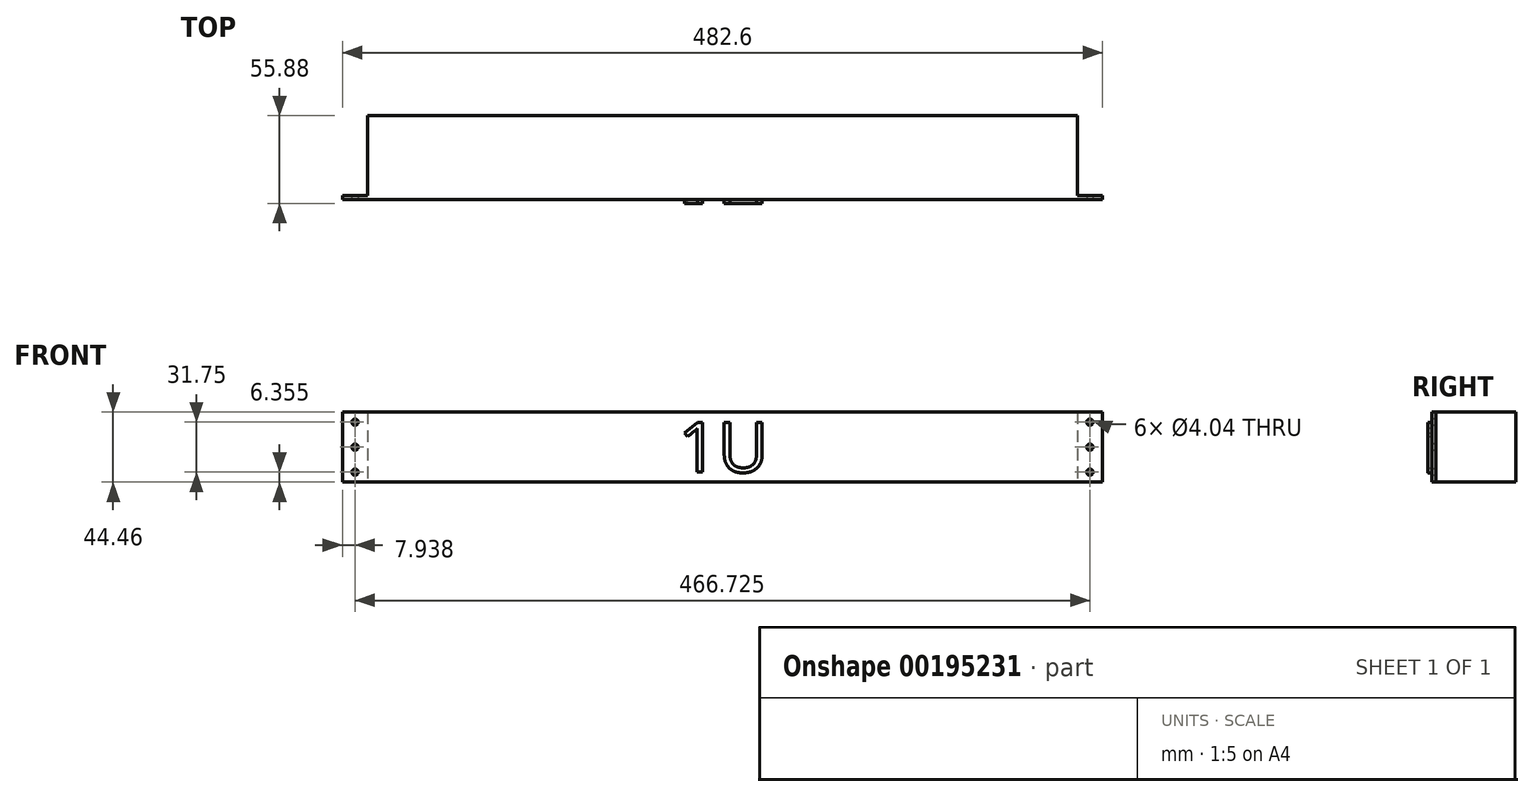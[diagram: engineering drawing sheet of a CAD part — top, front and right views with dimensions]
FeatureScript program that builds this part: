
annotation { "Feature Type Name" : "Feature", "Feature Type Description" : "" }
export const myFeature = defineFeature(function(context is Context, id is Id, definition is map)
    precondition{}
    {
        {
            var Q0;
            Q0=qCreatedBy(makeId("Front.planeOp"),FACE);
            var sketch = newSketch(context, id + "F0", { "sketchPlane" : qUnion([Q0])});
            skLineSegment(sketch, "E0.bottom", {"start": v(-241.3, 22.22) * mm, "end": v(241.3, 22.22) * mm});
            skLineSegment(sketch, "E0.top", {"start": v(-241.3, -22.22) * mm, "end": v(241.3, -22.22) * mm});
            skLineSegment(sketch, "E0.left", {"start": v(-241.3, 22.22) * mm, "end": v(-241.3, -22.22) * mm});
            skLineSegment(sketch, "E0.right", {"start": v(241.3, 22.22) * mm, "end": v(241.3, -22.22) * mm});
            skPoint(sketch, "E0.middle", {"position": v(0, 0) * mm});
            skSolve(sketch);
        }
        {
            var Q0;
            Q0 = qSketchRegion(id + "F0", true);
            extrude(context, id + "F1", {"entities" : qUnion([Q0]), "depth" : 2.54 * mm});
        }
        {
            var Q0;
            Q0=makeQuery(id+"F1.opExtrude","CAP_FACE",FACE,{"disambiguationData":[OSD([sQuery(id+"F0.wireOp",EDGE,"E0.bottom"),sQuery(id+"F0.wireOp",EDGE,"E0.top"),sQuery(id+"F0.wireOp",EDGE,"E0.left"),sQuery(id+"F0.wireOp",EDGE,"E0.right")])],"isStart":true});
            var sketch = newSketch(context, id + "F2", { "sketchPlane" : qUnion([Q0])});
            skLineSegment(sketch, "E1.bottom", {"start": v(-225.43, 22.22) * mm, "end": v(225.42, 22.23) * mm});
            skLineSegment(sketch, "E1.top", {"start": v(-225.43, -22.23) * mm, "end": v(225.42, -22.23) * mm});
            skLineSegment(sketch, "E1.left", {"start": v(-225.43, 22.22) * mm, "end": v(-225.43, -22.23) * mm});
            skLineSegment(sketch, "E1.right", {"start": v(225.43, 22.23) * mm, "end": v(225.43, -22.23) * mm});
            skPoint(sketch, "E1.middle", {"position": v(0, 0) * mm});
            skSolve(sketch);
        }
        {
            var Q0;
            Q0 = qSketchRegion(id + "F2", true);
            extrude(context, id + "F3", {"entities" : qUnion([Q0]), "operationType" : NewBodyOperationType.ADD, "depth" : 50.8 * mm});
        }
        {
            var Q0;
            Q0=makeQuery(id+"F1.opExtrude","CAP_FACE",FACE,{"disambiguationData":[OSD([sQuery(id+"F0.wireOp",EDGE,"E0.bottom"),sQuery(id+"F0.wireOp",EDGE,"E0.top"),sQuery(id+"F0.wireOp",EDGE,"E0.left"),sQuery(id+"F0.wireOp",EDGE,"E0.right")])],"isStart":false});
            var sketch = newSketch(context, id + "F4", { "sketchPlane" : qUnion([Q0])});
            skPoint(sketch, "E2", {"position": v(-233.36, 15.87) * mm});
            skPoint(sketch, "E3", {"position": v(-233.36, 0) * mm});
            skPoint(sketch, "E4", {"position": v(-233.36, -15.88) * mm});
            skPoint(sketch, "E5.0.1.0", {"position": v(-233.36, -28.58) * mm});
            skPoint(sketch, "E5.0.1.1", {"position": v(-233.36, -44.45) * mm});
            skPoint(sketch, "E5.0.1.2", {"position": v(-233.36, -60.33) * mm});
            skPoint(sketch, "E5.1.0.0", {"position": v(233.36, 15.87) * mm});
            skPoint(sketch, "E5.1.0.1", {"position": v(233.36, 0) * mm});
            skPoint(sketch, "E5.1.0.2", {"position": v(233.36, -15.88) * mm});
            skPoint(sketch, "E5.1.1.0", {"position": v(233.36, -28.58) * mm});
            skPoint(sketch, "E5.1.1.1", {"position": v(233.36, -44.45) * mm});
            skPoint(sketch, "E5.1.1.2", {"position": v(233.36, -60.33) * mm});
            skLineSegment(sketch, "E5.direction1", {"start": v(-233.36, 15.87) * mm, "end": v(233.36, 15.87) * mm, "construction": true});
            skLineSegment(sketch, "E5.direction2", {"start": v(-233.36, 15.87) * mm, "end": v(-233.36, -28.58) * mm, "construction": true});
            skSolve(sketch);
        }
        {
            var Q0;
            Q0=sQuery(id+"F4.wireOp",VERTEX,"E5.0.1.1");
            var Q1;
            Q1=sQuery(id+"F4.wireOp",VERTEX,"E5.0.1.2");
            var Q2;
            Q2=sQuery(id+"F4.wireOp",VERTEX,"E5.1.0.0");
            var Q3;
            Q3=sQuery(id+"F4.wireOp",VERTEX,"E5.1.1.0");
            var Q4;
            Q4=sQuery(id+"F4.wireOp",VERTEX,"E5.1.1.1");
            var Q5;
            Q5=sQuery(id+"F4.wireOp",VERTEX,"E5.1.0.1");
            var Q6;
            Q6=sQuery(id+"F4.wireOp",VERTEX,"E5.1.1.2");
            var Q7;
            Q7=sQuery(id+"F4.wireOp",VERTEX,"E5.1.0.2");
            var Q8;
            Q8=sQuery(id+"F4.wireOp",VERTEX,"E2");
            var Q9;
            Q9=sQuery(id+"F4.wireOp",VERTEX,"E3");
            var Q10;
            Q10=sQuery(id+"F4.wireOp",VERTEX,"E4");
            var Q11;
            Q11=sQuery(id+"F4.wireOp",VERTEX,"E5.0.1.0");
            var Q12;
            Q12=makeQuery(id+"F1.opExtrude","SWEPT_BODY",BODY,{"disambiguationData":[OSD([sQuery(id+"F0.wireOp",EDGE,"E0.bottom"),sQuery(id+"F0.wireOp",EDGE,"E0.top"),sQuery(id+"F0.wireOp",EDGE,"E0.left"),sQuery(id+"F0.wireOp",EDGE,"E0.right")])]});
            hole(context, id + "F5", {"style" : HoleStyle.SIMPLE, "endStyle" : HoleEndStyle.THROUGH, "standardTappedOrClearance" : lookupTablePath({ "standard" : "ANSI", "engagement" : "75%", "pitch" : "32 tpi", "size" : "#10", "type" : "Tapped" }), "standardBlindInLast" : lookupTablePath({ "standard" : "ANSI", "engagement" : "75%", "pitch" : "32 tpi", "size" : "#10", "type" : "Tapped" }), "holeDiameter" : 4.04 * mm, "locations" : qUnion([Q0, Q1, Q2, Q3, Q4, Q5, Q6, Q7, Q8, Q9, Q10, Q11]), "scope" : qUnion([Q12]), "isTappedThrough" : true, "majorDiameter" : 4.83 * mm, "showTappedDepth" : true});
        }
        {
            var Q0;
            Q0=makeQuery(id+"F1.opExtrude","CAP_FACE",FACE,{"disambiguationData":[OSD([sQuery(id+"F0.wireOp",EDGE,"E0.bottom"),sQuery(id+"F0.wireOp",EDGE,"E0.top"),sQuery(id+"F0.wireOp",EDGE,"E0.left"),sQuery(id+"F0.wireOp",EDGE,"E0.right")])],"isStart":false});
            var sketch = newSketch(context, id + "F6", { "sketchPlane" : qUnion([Q0])});
            skText(sketch, "E6", { "text": "1U", "fontName": "OpenSans-Regular.ttf"});
            const initialGuessF6  = {"E6": [-0.02808, -0.01587, 1, 0, 0.03175]};
            skSetInitialGuess(sketch, initialGuessF6);
            skSolve(sketch);
        }
        {
            var Q0;
            Q0 = qSketchRegion(id + "F6", true);
            extrude(context, id + "F7", {"entities" : qUnion([Q0]), "operationType" : NewBodyOperationType.ADD, "depth" : 2.54 * mm});
        }
    });
